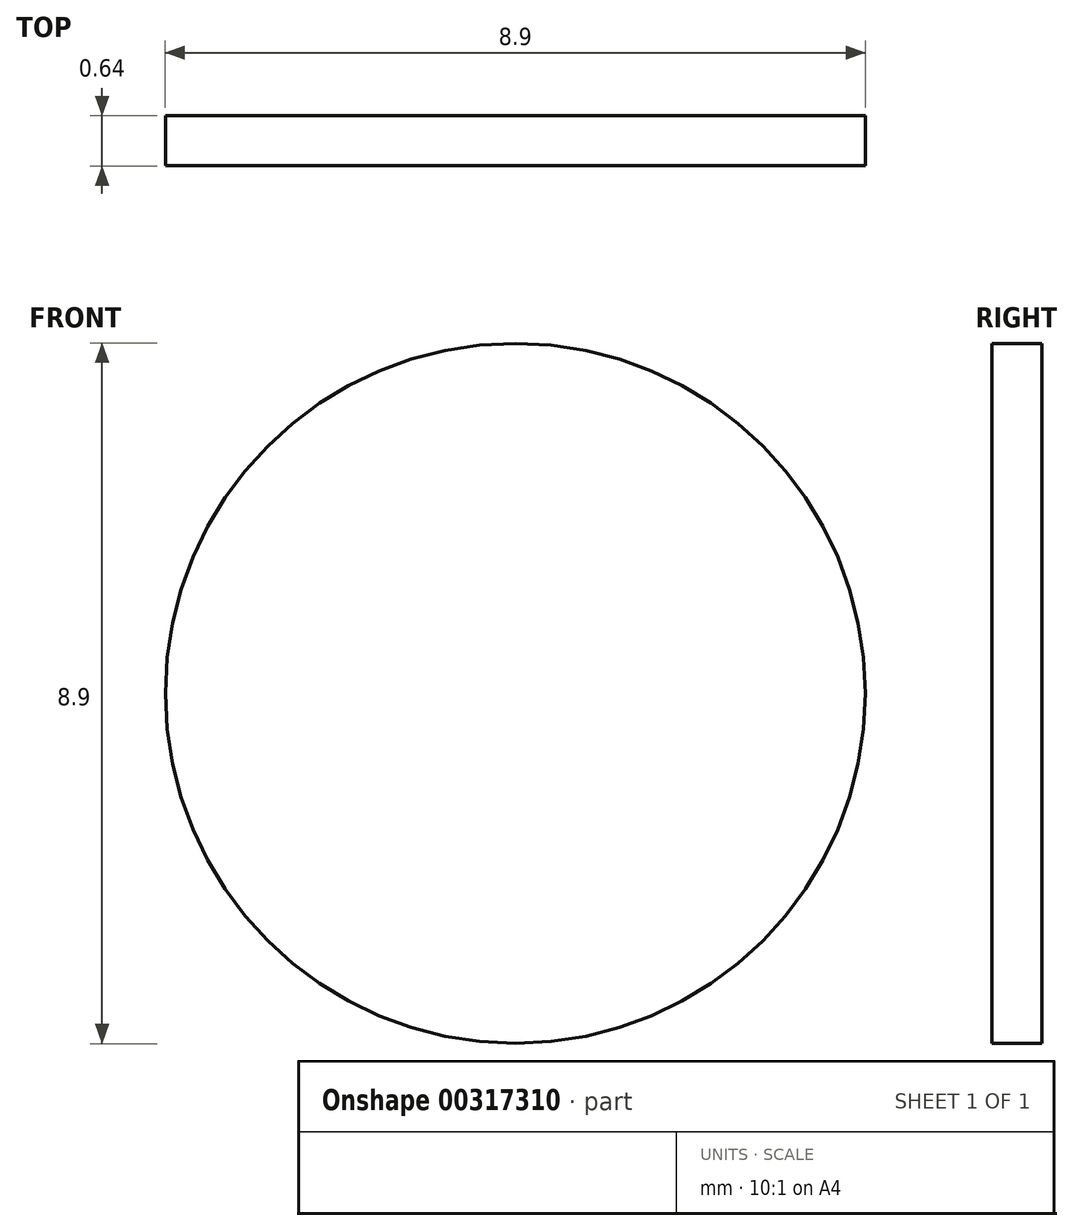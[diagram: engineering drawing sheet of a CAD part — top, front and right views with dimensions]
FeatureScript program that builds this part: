
annotation { "Feature Type Name" : "Feature", "Feature Type Description" : "" }
export const myFeature = defineFeature(function(context is Context, id is Id, definition is map)
    precondition{}
    {
        {
            var Q0;
            Q0=qCreatedBy(makeId("Front.planeOp"),FACE);
            var sketch = newSketch(context, id + "F0", { "sketchPlane" : qUnion([Q0])});
            skCircle(sketch, "E0", {"center": v(0, 0) * mm, "radius": 4.45 * mm});
            skSolve(sketch);
        }
        {
            var Q0;
            Q0=makeQuery(id+"F0.imprint","IMPRINT",FACE,{"disambiguationData":[TD([[makeQuery(id+"F0.imprint","IMPRINT",EDGE,{"derivedFrom":sQuery(id+"F0.wireOp",EDGE,"E0")}),1.0]])]});
            extrude(context, id + "F1", {"entities" : qUnion([Q0]), "depth" : 0.64 * mm});
        }
    });
